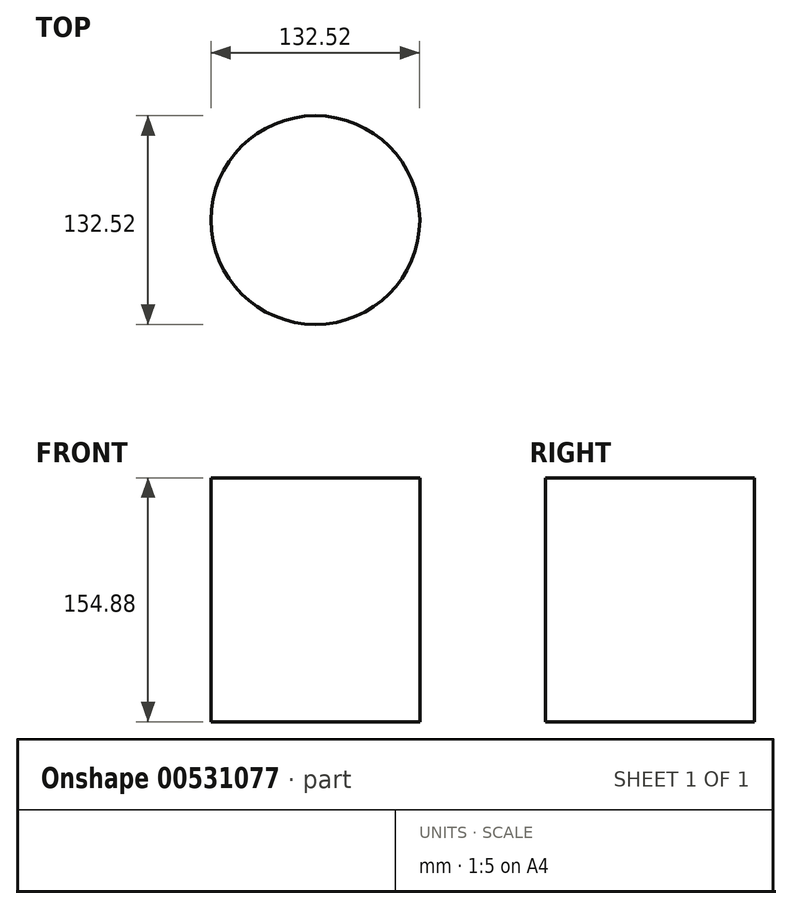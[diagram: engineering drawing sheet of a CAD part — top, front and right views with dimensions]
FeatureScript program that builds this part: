
annotation { "Feature Type Name" : "Feature", "Feature Type Description" : "" }
export const myFeature = defineFeature(function(context is Context, id is Id, definition is map)
    precondition{}
    {
        {
            var Q0;
            Q0=qCreatedBy(makeId("Top.planeOp"),FACE);
            var sketch = newSketch(context, id + "F0", { "sketchPlane" : qUnion([Q0])});
            skCircle(sketch, "E0", {"center": v(0, 8.3) * mm, "radius": 66.26 * mm});
            skSolve(sketch);
        }
        {
            var Q0;
            Q0 = qSketchRegion(id + "F0", true);
            extrude(context, id + "F1", {"entities" : qUnion([Q0]), "oppositeDirection" : true, "depth" : 154.88 * mm, "offsetDistance" : 25.4 * mm});
        }
    });
